# Revit family: ГРЕЕРС Д1
name_source: partatom
category: Обобщенные модели
revit_build: Autodesk Revit 2017 (Build: 20161006_0315(x64)
units: mm (PartAtom-declared; Revit-internal decimal feet)

## family parameters
Может служить основой для арматурных стержней = Нет
Общий = Нет
Основа = Грань
При загрузке вырезать с полостями = Нет
Размер круглого соединителя = Использовать диаметр
Тип детали = Нормальный
Точка расчета площади = Нет

## types (3) — shared parameters
URL = https://greers.ru
Вентилятор = Осевой, однофазный, переменного тока, с 3-х скоростным двигателем
Вес аппарата = 10.10 кг
Группа модели = ГРЕЕРС Д1
Изготовитель = ООО "ЮНИО-ВЕНТ"
Класс защиты = IP 54
Классификация нагрузки = Двигатель
Коэффициент мощности = 1
Материал = EPP
Напряжение питания = 230 В
Описание = Дестратификатор воздуха
Отметка по умолчанию = 800 мм
Расстояние от перекрытия = 800 мм

## per-type parameters (varying)
| type | Максимальное потребление тока | Максимальный расход мощности | Полная установленная мощность | Производительность |
| ГРЕЕРС Д1 (1-я скорость) | 0 А | 50 Вт | 58 В·А | 1100.0 м³/ч |
| ГРЕЕРС Д1 (2-я скорость) | 0 А | 70 Вт | 69 В·А | 1700.0 м³/ч |
| ГРЕЕРС Д1 (3-я скорость) | 1 А | 115 Вт | 122 В·А | 5200.0 м³/ч |
